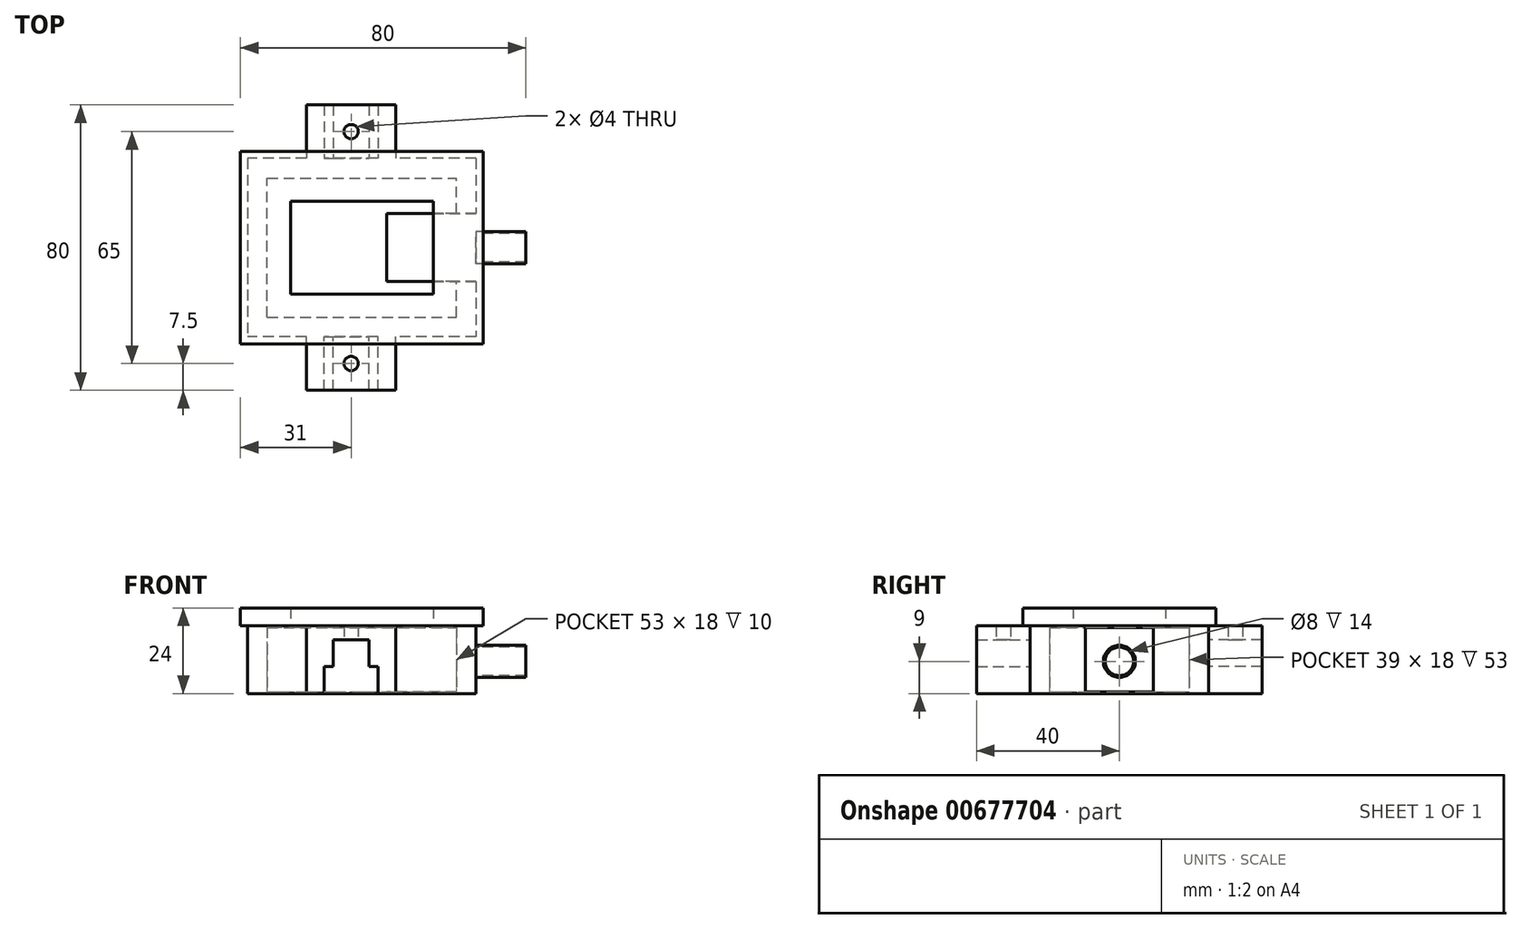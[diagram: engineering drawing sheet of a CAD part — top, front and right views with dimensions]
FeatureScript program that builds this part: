
annotation { "Feature Type Name" : "Feature", "Feature Type Description" : "" }
export const myFeature = defineFeature(function(context is Context, id is Id, definition is map)
    precondition{}
    {
        {
            var Q0;
            Q0=qCreatedBy(makeId("Front.planeOp"),FACE);
            var sketch = newSketch(context, id + "F0", { "sketchPlane" : qUnion([Q0])});
            skLineSegment(sketch, "E0", {"start": v(-24, 19) * mm, "end": v(30, 19) * mm});
            skLineSegment(sketch, "E1", {"start": v(-24, 19) * mm, "end": v(-24, 0) * mm});
            skLineSegment(sketch, "E2", {"start": v(-24, 0) * mm, "end": v(30, 0) * mm});
            skLineSegment(sketch, "E3", {"start": v(30, 0) * mm, "end": v(30, 19) * mm});
            skPoint(sketch, "E4", {"position": v(0, 0) * mm});
            skSolve(sketch);
        }
        {
            var Q0;
            Q0=makeQuery(id+"F0.imprint","IMPRINT",FACE,{"disambiguationData":[TD([[makeQuery(id+"F0.imprint","IMPRINT",EDGE,{"derivedFrom":sQuery(id+"F0.wireOp",EDGE,"E0")}),-1.0]])]});
            extrude(context, id + "F1", {"entities" : qUnion([Q0]), "depth" : 40 * mm, "offsetDistance" : 25 * mm, "symmetric" : true});
        }
        {
            var Q0;
            Q0=makeQuery(id+"F1.opExtrude","SWEPT_FACE",FACE,{"disambiguationData":[OSD([sQuery(id+"F0.wireOp",EDGE,"E3")])]});
            var sketch = newSketch(context, id + "F2", { "sketchPlane" : qUnion([Q0])});
            skLineSegment(sketch, "E5", {"start": v(-8.5, 0.5) * mm, "end": v(0, 0.5) * mm});
            skLineSegment(sketch, "E6", {"start": v(-8.5, 0.5) * mm, "end": v(-8.5, 17.5) * mm});
            skLineSegment(sketch, "E7", {"start": v(-8.5, 17.5) * mm, "end": v(0, 17.5) * mm});
            skLineSegment(sketch, "E8.MirrorCS", {"start": v(8.5, 17.5) * mm, "end": v(0, 17.5) * mm});
            skLineSegment(sketch, "E9.MirrorCS", {"start": v(8.5, 0.5) * mm, "end": v(8.5, 17.5) * mm});
            skLineSegment(sketch, "E10.MirrorCS", {"start": v(8.5, 0.5) * mm, "end": v(0, 0.5) * mm});
            skCircle(sketch, "E11", {"center": v(0, 9) * mm, "radius": 4.5 * mm});
            skPoint(sketch, "E12", {"position": v(-8.5, 9) * mm});
            skLineSegment(sketch, "E13", {"start": v(-8.5, 9) * mm, "end": v(8.5, 9) * mm, "construction": true});
            skSolve(sketch);
        }
        {
            var Q0;
            Q0=makeQuery(id+"F2.imprint","IMPRINT",FACE,{"disambiguationData":[TD([[makeQuery(id+"F2.imprint","IMPRINT",EDGE,{"derivedFrom":sQuery(id+"F2.wireOp",EDGE,"E5")}),1.0]])]});
            extrude(context, id + "F3", {"entities" : qUnion([Q0]), "operationType" : NewBodyOperationType.ADD, "depth" : 1.5 * mm, "offsetDistance" : 25 * mm});
        }
        {
            var Q0;
            Q0=makeQuery(id+"F3.boolean.opBoolean","SPLIT",FACE,{"disambiguationData":[TD([makeQuery(id+"F3.opExtrude","SWEPT_FACE",FACE,{"disambiguationData":[OSD([sQuery(id+"F2.wireOp",EDGE,"E11")])]})])],"derivedFrom":makeQuery(id+"F1.opExtrude","SWEPT_FACE",FACE,{"disambiguationData":[OSD([sQuery(id+"F0.wireOp",EDGE,"E3")])]})});
            extrude(context, id + "F4", {"entities" : qUnion([Q0]), "operationType" : NewBodyOperationType.ADD, "depth" : 19 * mm, "offsetDistance" : 25 * mm});
        }
        {
            var Q0;
            Q0=makeQuery(id+"F4.opExtrude","CAP_FACE",FACE,{"disambiguationData":[OSD([sQuery(id+"F0.wireOp",EDGE,"E3")])],"isStart":false});
            shell(context, id + "F5", {"entities" : qUnion([Q0]), "thickness" : .5 * mm});
        }
        {
            var Q0;
            Q0=makeQuery(id+"F1.opExtrude","SWEPT_FACE",FACE,{"disambiguationData":[OSD([sQuery(id+"F0.wireOp",EDGE,"E0")])]});
            var sketch = newSketch(context, id + "F6", { "sketchPlane" : qUnion([Q0])});
            skLineSegment(sketch, "E14.0", {"start": v(-29, 25) * mm, "end": v(35, 25) * mm});
            skLineSegment(sketch, "E14.1", {"start": v(-29, -25) * mm, "end": v(-29, 25) * mm});
            skLineSegment(sketch, "E15.0", {"start": v(35, -25) * mm, "end": v(35, 25) * mm});
            skLineSegment(sketch, "E15.1", {"start": v(-29, -25) * mm, "end": v(35, -25) * mm});
            skSolve(sketch);
        }
        {
            var Q0;
            Q0=makeQuery(id+"F6.imprint","IMPRINT",FACE,{"disambiguationData":[TD([[makeQuery(id+"F6.imprint","IMPRINT",EDGE,{"derivedFrom":sQuery(id+"F6.wireOp",EDGE,"E14.0")}),-1.0]])]});
            var Q1;
            Q1=qCreatedBy(makeId("Top.planeOp"),FACE);
            extrude(context, id + "F7", {"entities" : qUnion([Q0]), "endBound" : BoundingType.UP_TO_SURFACE, "oppositeDirection" : true, "depth" : 25 * mm, "endBoundEntityFace" : qUnion([Q1]), "offsetDistance" : 25 * mm});
        }
        {
            var Q0;
            Q0=makeQuery(id+"F7.opExtrude","SWEPT_FACE",FACE,{"disambiguationData":[OSD([sQuery(id+"F6.wireOp",EDGE,"E15.0")])]});
            var sketch = newSketch(context, id + "F8", { "sketchPlane" : qUnion([Q0])});
            skLineSegment(sketch, "E16.0", {"start": v(9.5, -0.5) * mm, "end": v(0, -0.5) * mm});
            skLineSegment(sketch, "E16.1", {"start": v(9.5, 19) * mm, "end": v(0, 19) * mm});
            skLineSegment(sketch, "E16.2", {"start": v(-9.5, 19) * mm, "end": v(0, 19) * mm});
            skLineSegment(sketch, "E16.3", {"start": v(9.5, -0.5) * mm, "end": v(9.5, 19) * mm});
            skLineSegment(sketch, "E16.4", {"start": v(-9.5, -0.5) * mm, "end": v(-9.5, 19) * mm});
            skLineSegment(sketch, "E16.5", {"start": v(-9.5, -0.5) * mm, "end": v(0, -0.5) * mm});
            skSolve(sketch);
        }
        {
            var Q0;
            Q0=qSketchRegion(id+"F8",true);
            var Q1;
            Q1=makeQuery(id+"F7.opExtrude","SWEPT_FACE",FACE,{"disambiguationData":[OSD([sQuery(id+"F6.wireOp",EDGE,"E15.0")])]});
            var Q2;
            Q2=makeQuery(id+"F1.opExtrude","SWEPT_BODY",BODY,{"disambiguationData":[OSD([sQuery(id+"F0.wireOp",EDGE,"E0"),sQuery(id+"F0.wireOp",EDGE,"E1"),sQuery(id+"F0.wireOp",EDGE,"E2"),sQuery(id+"F0.wireOp",EDGE,"E3")])]});
            extrude(context, id + "F9", {"entities" : qUnion([Q0]), "operationType" : NewBodyOperationType.REMOVE, "oppositeDirection" : true, "depth" : 25 * mm, "endBoundEntityFace" : qUnion([Q1]), "endBoundEntityBody" : qUnion([Q2]), "offsetDistance" : 25 * mm});
        }
        {
            var Q0;
            Q0=makeQuery(id+"F6.imprint","IMPRINT",FACE,{"disambiguationData":[TD([[makeQuery(id+"F6.imprint","IMPRINT",EDGE,{"derivedFrom":sQuery(id+"F6.wireOp",EDGE,"E14.0")}),-1.0]])]});
            var sketch = newSketch(context, id + "F10", { "sketchPlane" : qUnion([Q0])});
            skLineSegment(sketch, "E17.0", {"start": v(-31, 27) * mm, "end": v(37, 27) * mm});
            skLineSegment(sketch, "E17.1", {"start": v(-31, -27) * mm, "end": v(-31, 27) * mm});
            skLineSegment(sketch, "E17.2", {"start": v(-31, -27) * mm, "end": v(37, -27) * mm});
            skLineSegment(sketch, "E17.3", {"start": v(37, -27) * mm, "end": v(37, 27) * mm});
            skLineSegment(sketch, "E18.0", {"start": v(23, 13) * mm, "end": v(-17, 13) * mm});
            skLineSegment(sketch, "E18.1", {"start": v(23, -13) * mm, "end": v(23, 13) * mm});
            skLineSegment(sketch, "E18.2", {"start": v(-17, -13) * mm, "end": v(23, -13) * mm});
            skLineSegment(sketch, "E18.3", {"start": v(-17, 13) * mm, "end": v(-17, -13) * mm});
            skLineSegment(sketch, "E19", {"start": v(3, 27) * mm, "end": v(3, 20) * mm, "construction": true});
            skPoint(sketch, "E20", {"position": v(3, 25) * mm});
            skLineSegment(sketch, "E21", {"start": v(3, 25) * mm, "end": v(3, 20) * mm, "construction": true});
            skLineSegment(sketch, "E22", {"start": v(3, 22.5) * mm, "end": v(-7, 22.5) * mm, "construction": true});
            skLineSegment(sketch, "E23", {"start": v(-7, 22.5) * mm, "end": v(-7, 23.5) * mm});
            skLineSegment(sketch, "E24", {"start": v(-7, 23.5) * mm, "end": v(3, 23.5) * mm});
            skLineSegment(sketch, "E25.MirrorCS", {"start": v(-7, 21.5) * mm, "end": v(3, 21.5) * mm});
            skLineSegment(sketch, "E26.MirrorCS", {"start": v(-7, 22.5) * mm, "end": v(-7, 21.5) * mm});
            skLineSegment(sketch, "E27.MirrorCS", {"start": v(13, 23.5) * mm, "end": v(3, 23.5) * mm});
            skLineSegment(sketch, "E28.MirrorCS", {"start": v(13, 22.5) * mm, "end": v(13, 23.5) * mm});
            skLineSegment(sketch, "E29.MirrorCS", {"start": v(13, 21.5) * mm, "end": v(3, 21.5) * mm});
            skLineSegment(sketch, "E30.MirrorCS", {"start": v(13, 22.5) * mm, "end": v(13, 21.5) * mm});
            skLineSegment(sketch, "E31.0", {"start": v(-7.05, 22.5) * mm, "end": v(-7.05, 23.55) * mm});
            skLineSegment(sketch, "E31.1", {"start": v(-7.05, 22.5) * mm, "end": v(-7.05, 21.45) * mm});
            skLineSegment(sketch, "E31.2", {"start": v(-7.05, 23.55) * mm, "end": v(3, 23.55) * mm});
            skLineSegment(sketch, "E31.3", {"start": v(-7.05, 21.45) * mm, "end": v(3, 21.45) * mm});
            skLineSegment(sketch, "E31.4", {"start": v(13.05, 23.55) * mm, "end": v(3, 23.55) * mm});
            skLineSegment(sketch, "E31.5", {"start": v(13.05, 22.5) * mm, "end": v(13.05, 23.55) * mm});
            skLineSegment(sketch, "E31.6", {"start": v(13.05, 22.5) * mm, "end": v(13.05, 21.45) * mm});
            skLineSegment(sketch, "E31.7", {"start": v(13.05, 21.45) * mm, "end": v(3, 21.45) * mm});
            skLineSegment(sketch, "E32", {"start": v(-31, 0) * mm, "end": v(37, 0) * mm, "construction": true});
            skLineSegment(sketch, "E33.MirrorCS", {"start": v(-7, -22.5) * mm, "end": v(-7, -23.5) * mm});
            skLineSegment(sketch, "E34.MirrorCS", {"start": v(-7, -22.5) * mm, "end": v(-7, -21.5) * mm});
            skLineSegment(sketch, "E35.MirrorCS", {"start": v(-7, -21.5) * mm, "end": v(3, -21.5) * mm});
            skLineSegment(sketch, "E36.MirrorCS", {"start": v(-7, -23.5) * mm, "end": v(3, -23.5) * mm});
            skLineSegment(sketch, "E37.MirrorCS", {"start": v(13, -23.5) * mm, "end": v(3, -23.5) * mm});
            skLineSegment(sketch, "E38.MirrorCS", {"start": v(13, -21.5) * mm, "end": v(3, -21.5) * mm});
            skLineSegment(sketch, "E39.MirrorCS", {"start": v(13, -22.5) * mm, "end": v(13, -23.5) * mm});
            skLineSegment(sketch, "E40.MirrorCS", {"start": v(13, -22.5) * mm, "end": v(13, -21.5) * mm});
            skLineSegment(sketch, "E41.0", {"start": v(13.05, -22.5) * mm, "end": v(13.05, -23.55) * mm});
            skLineSegment(sketch, "E41.1", {"start": v(13.05, -22.5) * mm, "end": v(13.05, -21.45) * mm});
            skLineSegment(sketch, "E41.2", {"start": v(13.05, -23.55) * mm, "end": v(3, -23.55) * mm});
            skLineSegment(sketch, "E41.3", {"start": v(13.05, -21.45) * mm, "end": v(3, -21.45) * mm});
            skLineSegment(sketch, "E41.4", {"start": v(-7.05, -23.55) * mm, "end": v(3, -23.55) * mm});
            skLineSegment(sketch, "E41.5", {"start": v(-7.05, -22.5) * mm, "end": v(-7.05, -23.55) * mm});
            skLineSegment(sketch, "E41.6", {"start": v(-7.05, -22.5) * mm, "end": v(-7.05, -21.45) * mm});
            skLineSegment(sketch, "E41.7", {"start": v(-7.05, -21.45) * mm, "end": v(3, -21.45) * mm});
            skLineSegment(sketch, "E42", {"start": v(-31, -27) * mm, "end": v(-29.4, -25.4) * mm, "construction": true});
            skLineSegment(sketch, "E43", {"start": v(-31, 0) * mm, "end": v(-24.69, 0) * mm, "construction": true});
            skPoint(sketch, "E44", {"position": v(-29, 0) * mm});
            skLineSegment(sketch, "E45", {"start": v(-29, 0) * mm, "end": v(-24.69, 0) * mm, "construction": true});
            skLineSegment(sketch, "E46", {"start": v(-26.84, 0) * mm, "end": v(-26.84, -10) * mm, "construction": true});
            skLineSegment(sketch, "E47", {"start": v(-26.84, -10) * mm, "end": v(-27.9, -10) * mm});
            skLineSegment(sketch, "E48", {"start": v(-27.9, -10) * mm, "end": v(-27.9, 0) * mm});
            skLineSegment(sketch, "E49.MirrorCS", {"start": v(-25.78, -10) * mm, "end": v(-25.78, 0) * mm});
            skLineSegment(sketch, "E50.MirrorCS", {"start": v(-26.84, -10) * mm, "end": v(-25.78, -10) * mm});
            skLineSegment(sketch, "E51.MirrorCS", {"start": v(-27.9, 10) * mm, "end": v(-27.9, 0) * mm});
            skLineSegment(sketch, "E52.MirrorCS", {"start": v(-25.78, 10) * mm, "end": v(-25.78, 0) * mm});
            skLineSegment(sketch, "E53.MirrorCS", {"start": v(-26.84, 10) * mm, "end": v(-25.78, 10) * mm});
            skLineSegment(sketch, "E54.MirrorCS", {"start": v(-26.84, 10) * mm, "end": v(-27.9, 10) * mm});
            skSolve(sketch);
        }
        {
            var Q0;
            Q0=makeQuery(id+"F10.imprint","IMPRINT",FACE,{"disambiguationData":[TD([[makeQuery(id+"F10.imprint","IMPRINT",EDGE,{"derivedFrom":sQuery(id+"F10.wireOp",EDGE,"E17.0")}),-1.0]])]});
            var Q1;
            Q1=makeQuery(id+"F6.imprint","IMPRINT",FACE,{"disambiguationData":[TD([[makeQuery(id+"F6.imprint","IMPRINT",EDGE,{"derivedFrom":sQuery(id+"F6.wireOp",EDGE,"E14.0")}),-1.0]])]});
            var Q2;
            Q2=makeQuery(id+"F10.imprint","IMPRINT",FACE,{"disambiguationData":[TD([[makeQuery(id+"F10.imprint","IMPRINT",EDGE,{"derivedFrom":sQuery(id+"F10.wireOp",EDGE,"E18.0")}),-1.0]])]});
            var Q3;
            Q3=sQuery(id+"F10.wireOp",EDGE,"E17.1");
            var Q4;
            Q4=sQuery(id+"F10.wireOp",EDGE,"E17.2");
            var Q5;
            Q5=sQuery(id+"F10.wireOp",EDGE,"E17.3");
            var Q6;
            Q6=sQuery(id+"F10.wireOp",EDGE,"E17.0");
            var Q7;
            Q7=sQuery(id+"F10.wireOp",EDGE,"E18.0");
            var Q8;
            Q8=sQuery(id+"F10.wireOp",EDGE,"E18.1");
            var Q9;
            Q9=sQuery(id+"F10.wireOp",EDGE,"E18.2");
            var Q10;
            Q10=sQuery(id+"F10.wireOp",EDGE,"E18.3");
            extrude(context, id + "F11", {"entities" : qUnion([Q0, Q1, Q2]), "surfaceEntities" : qUnion([Q3, Q4, Q5, Q6, Q7, Q8, Q9, Q10]), "depth" : 5 * mm, "offsetDistance" : 25 * mm});
        }
        {
            var Q0;
            Q0=makeQuery(id+"F7.opExtrude","SWEPT_FACE",FACE,{"disambiguationData":[OSD([sQuery(id+"F6.wireOp",EDGE,"E14.0")])]});
            var sketch = newSketch(context, id + "F12", { "sketchPlane" : qUnion([Q0])});
            skLineSegment(sketch, "E55", {"start": v(0, 15) * mm, "end": v(-5, 15) * mm});
            skLineSegment(sketch, "E56", {"start": v(-5, 15) * mm, "end": v(-5, 0) * mm});
            skLineSegment(sketch, "E57", {"start": v(0, 19) * mm, "end": v(0, 0) * mm, "construction": true});
            skLineSegment(sketch, "E58.MirrorCS", {"start": v(0, 15) * mm, "end": v(5, 15) * mm});
            skLineSegment(sketch, "E59.MirrorCS", {"start": v(5, 15) * mm, "end": v(5, 0) * mm});
            skLineSegment(sketch, "E60", {"start": v(-5, 7.5) * mm, "end": v(-7.5, 7.5) * mm});
            skLineSegment(sketch, "E61", {"start": v(-7.5, 7.5) * mm, "end": v(-7.5, 0) * mm});
            skLineSegment(sketch, "E62.MirrorCS", {"start": v(5, 7.5) * mm, "end": v(7.5, 7.5) * mm});
            skLineSegment(sketch, "E63.MirrorCS", {"start": v(7.5, 7.5) * mm, "end": v(7.5, 0) * mm});
            skLineSegment(sketch, "E64", {"start": v(0, 19) * mm, "end": v(-12.5, 19) * mm});
            skLineSegment(sketch, "E65", {"start": v(-12.5, 19) * mm, "end": v(-12.5, 0) * mm});
            skLineSegment(sketch, "E66.MirrorCS", {"start": v(0, 19) * mm, "end": v(12.5, 19) * mm});
            skLineSegment(sketch, "E67.MirrorCS", {"start": v(12.5, 19) * mm, "end": v(12.5, 0) * mm});
            skLineSegment(sketch, "E68.0", {"start": v(-7.55, 7.6) * mm, "end": v(-7.55, 0) * mm});
            skLineSegment(sketch, "E69.0", {"start": v(0, 15.1) * mm, "end": v(-5.05, 15.1) * mm});
            skLineSegment(sketch, "E70", {"start": v(-5.05, 15.1) * mm, "end": v(-5.05, 7.6) * mm});
            skLineSegment(sketch, "E71", {"start": v(-7.55, 7.6) * mm, "end": v(-5.05, 7.6) * mm});
            skLineSegment(sketch, "E72.MirrorCS", {"start": v(0, 15.1) * mm, "end": v(5.05, 15.1) * mm});
            skLineSegment(sketch, "E73.MirrorCS", {"start": v(5.05, 15.1) * mm, "end": v(5.05, 7.6) * mm});
            skLineSegment(sketch, "E74.MirrorCS", {"start": v(7.55, 7.6) * mm, "end": v(5.05, 7.6) * mm});
            skLineSegment(sketch, "E75.MirrorCS", {"start": v(7.55, 7.6) * mm, "end": v(7.55, 0) * mm});
            skSolve(sketch);
        }
        {
            var Q0;
            Q0=qCreatedBy(makeId("Top.planeOp"),FACE);
            cPlane(context, id + "F13", {"entities" : qUnion([Q0]), "cplaneType" : CPlaneType.OFFSET, "offset" : 8 * mm, "oppositeDirection" : true, "width" : 150 * mm, "height" : 150 * mm});
        }
        {
            var Q0;
            Q0=makeQuery(id+"F12.imprint","IMPRINT",FACE,{"disambiguationData":[TD([[makeQuery(id+"F12.imprint","IMPRINT",EDGE,{"derivedFrom":sQuery(id+"F12.wireOp",EDGE,"E64")}),1.0]])]});
            extrude(context, id + "F14", {"entities" : qUnion([Q0]), "operationType" : NewBodyOperationType.ADD, "depth" : 15 * mm, "offsetDistance" : 25 * mm});
        }
        {
            var Q0;
            Q0=makeQuery(id+"F14.opExtrude","SWEPT_FACE",FACE,{"disambiguationData":[OSD([sQuery(id+"F12.wireOp",EDGE,"E69.0"),sQuery(id+"F12.wireOp",EDGE,"E72.MirrorCS")])]});
            var sketch = newSketch(context, id + "F15", { "sketchPlane" : qUnion([Q0])});
            skCircle(sketch, "E76.cCircle", {"center": v(0, -32.5) * mm, "radius": 3.5 * mm, "construction": true});
            skLineSegment(sketch, "E76.0", {"start": v(0, -29) * mm, "end": v(3.03, -30.75) * mm});
            skLineSegment(sketch, "E76.1", {"start": v(3.03, -30.75) * mm, "end": v(3.03, -34.25) * mm});
            skLineSegment(sketch, "E76.2", {"start": v(3.03, -34.25) * mm, "end": v(0, -36) * mm});
            skLineSegment(sketch, "E76.3", {"start": v(0, -36) * mm, "end": v(-3.03, -34.25) * mm});
            skLineSegment(sketch, "E76.4", {"start": v(-3.03, -34.25) * mm, "end": v(-3.03, -30.75) * mm});
            skLineSegment(sketch, "E76.5", {"start": v(-3.03, -30.75) * mm, "end": v(0, -29) * mm});
            skCircle(sketch, "E77", {"center": v(0, -32.5) * mm, "radius": 2 * mm});
            skLineSegment(sketch, "E78", {"start": v(0, -25) * mm, "end": v(0, -40) * mm, "construction": true});
            skSolve(sketch);
        }
        {
            var Q0;
            Q0=makeQuery(id+"F15.imprint","IMPRINT",FACE,{"disambiguationData":[TD([[makeQuery(id+"F15.imprint","IMPRINT",EDGE,{"derivedFrom":sQuery(id+"F15.wireOp",EDGE,"E77")}),1.0]])]});
            var Q1;
            Q1=sQuery(id+"F15.wireOp",EDGE,"E77");
            extrude(context, id + "F16", {"entities" : qUnion([Q0]), "operationType" : NewBodyOperationType.REMOVE, "surfaceEntities" : qUnion([Q1]), "endBound" : BoundingType.THROUGH_ALL, "oppositeDirection" : true, "depth" : 25 * mm, "offsetDistance" : 25 * mm});
        }
        {
            var Q0;
            Q0=makeQuery(id+"F7.opExtrude","SWEPT_BODY",BODY,{"disambiguationData":[OSD([sQuery(id+"F0.wireOp",EDGE,"E0"),sQuery(id+"F0.wireOp",EDGE,"E1"),sQuery(id+"F0.wireOp",EDGE,"E3"),sQuery(id+"F6.wireOp",EDGE,"E14.0"),sQuery(id+"F6.wireOp",EDGE,"E14.1"),sQuery(id+"F6.wireOp",EDGE,"E15.0"),sQuery(id+"F6.wireOp",EDGE,"E15.1")])]});
            var Q1;
            Q1=qCreatedBy(makeId("Front.planeOp"),FACE);
            mirror(context, id + "F17", {"operationType" : NewBodyOperationType.ADD, "entities" : qUnion([Q0]), "mirrorPlane" : qUnion([Q1])});
        }
    });
